# Revit family: Clarus_Flex Mobile_R18
name_source: partatom
category: Furniture
revit_build: Autodesk Revit 2018 (Build: 20190510_1515(x64)
units: mm (PartAtom-declared; Revit-internal decimal feet)

## family parameters
Cut with Voids When Loaded = No
Host = Face
Room Calculation Point = No
Shared = No

## types (2) — shared parameters
Caster Base = Clarus Black
Default Elevation = 0"
Depth = 22"
Description = Flex Mobile is the most elegant, functional glassboard on wheels ever brought to market. Its wide, strong base gives Flex an Eiffel Tower elegance, while providing increased functionality and stability to the writable glassboard.
Height = 78"
Manufacturer = Clarus
Model = Flex Mobile
Modeled By = Commense Studio
Product URL = https://www.clarus.com
URL = https://www.clarus.com

## per-type parameters (varying)
| type | Width |
| Mediium 40" X 78" X 22" | 40" |
| Large 60" X 78" X 22" | 60" |

## geometry (parser evidence)
native form markers: Blend x28, Sweep x11
no freeform markers — native parametric forms only
